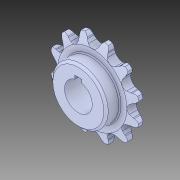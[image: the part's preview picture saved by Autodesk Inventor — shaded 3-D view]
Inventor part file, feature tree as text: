
AUTODESK INVENTOR PART (.ipt)
format: ipt  version: 2019 (Build 230136000, 136)  size: 358,912 bytes
history: native  units: in
note: dims shown in document units (in); Inventor stores cm internally (conversion verified against a paired STEP export)
features: chamfer x1
ambient origin geometry x8: Origin, YZ Plane, XZ Plane, XY Plane, X Axis, Y Axis, Z Axis, Center Point
bodies: Solid1 (feature_tree)
feature tree (1):
  chamfer  "Chamfer1"  [1 undecoded]
note: 1 required parameter value undecoded (feature->parameter linkage not recoverable at this tier; creation-order binding heuristic only, values carry confidence <= 0.55)
